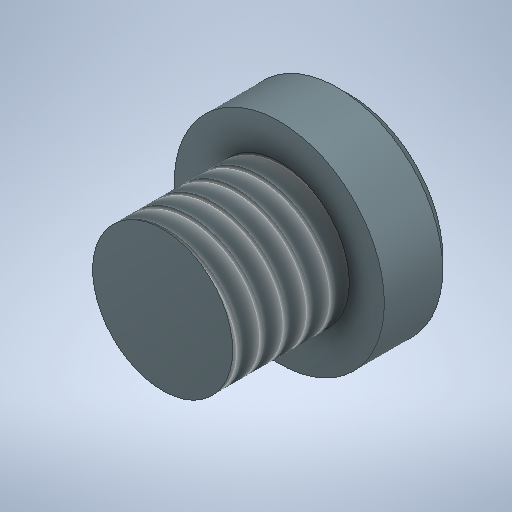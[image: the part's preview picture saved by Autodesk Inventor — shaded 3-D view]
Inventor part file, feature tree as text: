
AUTODESK INVENTOR PART (.ipt)
format: ipt  version: 2025.1 (Build 291241000, 241)  size: 287,744 bytes
history: native  units: mm
features: revolve x1, thread x1, chamfer x1, sketch x1
ambient origin geometry x8: Origin, YZ Plane, XZ Plane, XY Plane, X Axis, Y Axis, Z Axis, Center Point
bodies: Solid1 (feature_tree)
feature tree (4):
  revolve  "Revolution1"  [1 undecoded]
  thread  "Thread1"  [1 undecoded]
  chamfer  "Chamfer1"  Distance=3.0mm
  sketch  "Sketch1"  dims[d0=9.0mm d1=6.0mm d2=5.0mm d3=3.0mm d4=90.0deg d5=5.0mm d6=0.0mm d7=0.5mm d8=2.0mm d9=45.0deg]
note: 2 required parameter values undecoded (feature->parameter linkage not recoverable at this tier; creation-order binding heuristic only, values carry confidence <= 0.55)